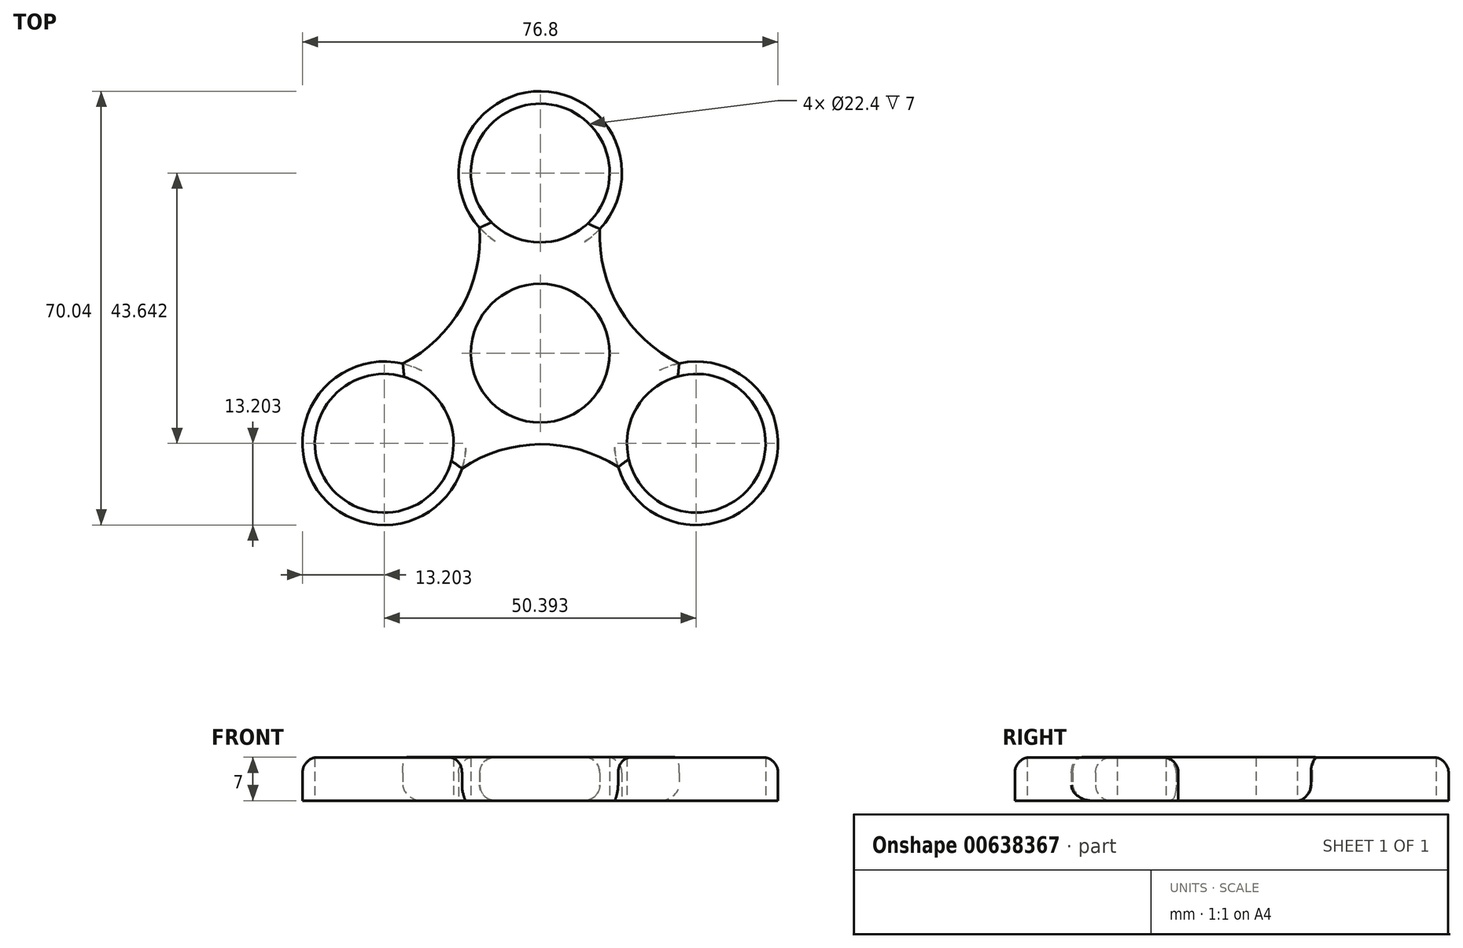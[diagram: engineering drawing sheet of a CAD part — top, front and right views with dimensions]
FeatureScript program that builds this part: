
annotation { "Feature Type Name" : "Feature", "Feature Type Description" : "" }
export const myFeature = defineFeature(function(context is Context, id is Id, definition is map)
    precondition{}
    {
        {
            var Q0;
            Q0=qCreatedBy(makeId("Top.planeOp"),FACE);
            var sketch = newSketch(context, id + "F0", { "sketchPlane" : qUnion([Q0])});
            skCircle(sketch, "E0", {"center": v(0, 0) * mm, "radius": 11.2 * mm});
            skCircle(sketch, "E1", {"center": v(0, 29.1) * mm, "radius": 11.2 * mm});
            skArc(sketch, "E2", {"start": v(9.63, 20.07) * mm, "mid": v(0.13, 42.3) * mm, "end": v(-9.8, 20.26) * mm});
            skCircle(sketch, "E3.1.0", {"center": v(-25.2, -14.55) * mm, "radius": 11.2 * mm});
            skArc(sketch, "E3.1.1", {"start": v(-22.2, -1.7) * mm, "mid": v(-36.7, -21.04) * mm, "end": v(-12.64, -18.62) * mm});
            skCircle(sketch, "E3.2.0", {"center": v(25.2, -14.55) * mm, "radius": 11.2 * mm});
            skArc(sketch, "E3.2.1", {"start": v(12.56, -18.38) * mm, "mid": v(36.56, -21.26) * mm, "end": v(22.45, -1.64) * mm});
            skArc(sketch, "E4", {"start": v(9.63, 20.07) * mm, "mid": v(12.78, 7.3) * mm, "end": v(22.45, -1.64) * mm});
            skArc(sketch, "E5.1.0", {"start": v(-22.2, -1.7) * mm, "mid": v(-12.7, 7.42) * mm, "end": v(-9.8, 20.26) * mm});
            skArc(sketch, "E5.2.0", {"start": v(12.56, -18.38) * mm, "mid": v(-0.07, -14.7) * mm, "end": v(-12.64, -18.62) * mm});
            skSolve(sketch);
        }
        {
            var Q0;
            Q0 = qSketchRegion(id + "F0", true);
            extrude(context, id + "F1", {"entities" : qUnion([Q0]), "depth" : 7 * mm, "offsetDistance" : 25 * mm});
        }
        {
            var Q0;
            Q0=makeQuery(id+"F1.opExtrude","CAP_EDGE",EDGE,{"disambiguationData":[OSD([sQuery(id+"F0.wireOp",EDGE,"E2")])],"isStart":false});
            var Q1;
            Q1=makeQuery(id+"F1.opExtrude","CAP_EDGE",EDGE,{"disambiguationData":[OSD([sQuery(id+"F0.wireOp",EDGE,"E4")])],"isStart":false});
            var Q2;
            Q2=makeQuery(id+"F1.opExtrude","CAP_EDGE",EDGE,{"disambiguationData":[OSD([sQuery(id+"F0.wireOp",EDGE,"E3.2.1")])],"isStart":false});
            var Q3;
            Q3=makeQuery(id+"F1.opExtrude","CAP_EDGE",EDGE,{"disambiguationData":[OSD([sQuery(id+"F0.wireOp",EDGE,"E5.2.0")])],"isStart":false});
            var Q4;
            Q4=makeQuery(id+"F1.opExtrude","CAP_EDGE",EDGE,{"disambiguationData":[OSD([sQuery(id+"F0.wireOp",EDGE,"E3.1.1")])],"isStart":false});
            var Q5;
            Q5=makeQuery(id+"F1.opExtrude","CAP_EDGE",EDGE,{"disambiguationData":[OSD([sQuery(id+"F0.wireOp",EDGE,"E5.1.0")])],"isStart":false});
            fillet(context, id + "F2", {"entities" : qUnion([Q0, Q1, Q2, Q3, Q4, Q5]), "radius" : 2.5 * mm, "tangentPropagation" : true, "allowEdgeOverflow" : false});
        }
        {
            var Q0;
            Q0=makeQuery(id+"F1.opExtrude","CAP_EDGE",EDGE,{"disambiguationData":[OSD([sQuery(id+"F0.wireOp",EDGE,"E4")])],"isStart":true});
            var Q1;
            Q1=makeQuery(id+"F1.opExtrude","CAP_EDGE",EDGE,{"disambiguationData":[OSD([sQuery(id+"F0.wireOp",EDGE,"E5.1.0")])],"isStart":true});
            var Q2;
            Q2=makeQuery(id+"F1.opExtrude","CAP_EDGE",EDGE,{"disambiguationData":[OSD([sQuery(id+"F0.wireOp",EDGE,"E5.2.0")])],"isStart":true});
            fillet(context, id + "F3", {"entities" : qUnion([Q0, Q1, Q2]), "radius" : 2.5 * mm, "tangentPropagation" : true, "allowEdgeOverflow" : false});
        }
    });
